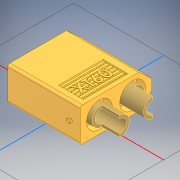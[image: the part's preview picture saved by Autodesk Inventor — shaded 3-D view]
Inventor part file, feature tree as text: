
AUTODESK INVENTOR PART (.ipt)
format: ipt  version: 2022 (Build 260153000, 153)  size: 682,496 bytes
history: native  units: mm
features: other x5, fillet x1
ambient origin geometry x8: Origin, YZ Plane, XZ Plane, XY Plane, X Axis, Y Axis, Z Axis, Center Point
bodies: Body1 (feature_tree), Body2 (feature_tree), Body3 (feature_tree)
feature tree (6):
  other  "Твердое тело1"
  other  "Твердое тело2"
  other  "Твердое тело3"
  other  "Cut-Extrude6"
  other  "Body-Move_Copy3"
  fillet  "Fillet3"  [1 undecoded]
note: 1 required parameter value undecoded (feature->parameter linkage not recoverable at this tier; creation-order binding heuristic only, values carry confidence <= 0.55)
